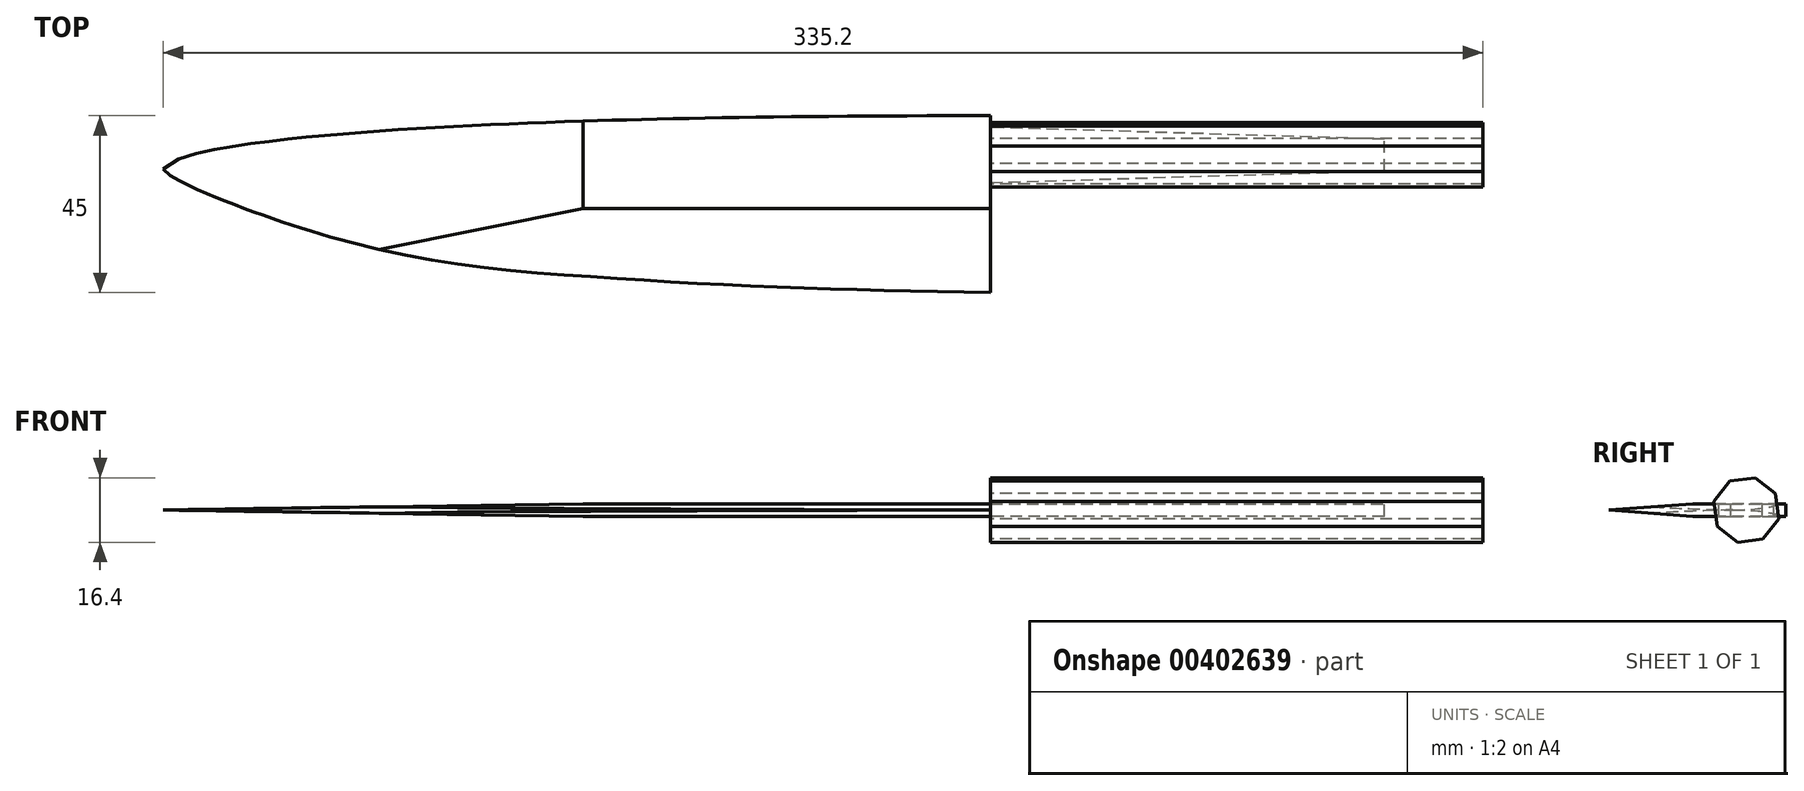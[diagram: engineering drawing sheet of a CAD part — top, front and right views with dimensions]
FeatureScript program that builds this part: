
annotation { "Feature Type Name" : "Feature", "Feature Type Description" : "" }
export const myFeature = defineFeature(function(context is Context, id is Id, definition is map)
    precondition{}
    {
        {
            var Q0;
            Q0=qCreatedBy(makeId("Top.planeOp"),FACE);
            var sketch = newSketch(context, id + "F0", { "sketchPlane" : qUnion([Q0])});
            skFitSpline(sketch, "E0", {"points": [v(0, 17) * mm, v(-209.96, 4) * mm, v(-210, 3) * mm, v(-163.2, -15.06) * mm, v(-98.97, -24.11) * mm, v(0, -28) * mm], "startDerivative": vector(-1422.34, 0) * mm, "endDerivative": vector(667.4, -12.24) * mm});
            skLineSegment(sketch, "E1", {"start": v(0, -28) * mm, "end": v(0, 0) * mm});
            skLineSegment(sketch, "E2", {"start": v(0, 0) * mm, "end": v(100, 3) * mm});
            skLineSegment(sketch, "E3", {"start": v(100, 3) * mm, "end": v(100, 11) * mm});
            skLineSegment(sketch, "E4", {"start": v(100, 11) * mm, "end": v(0, 14) * mm});
            skLineSegment(sketch, "E5", {"start": v(0, 14) * mm, "end": v(0, 17) * mm});
            skSolve(sketch);
        }
        {
            var Q0;
            Q0=makeQuery(id+"F0.imprint","IMPRINT",FACE,{"disambiguationData":[TD([[makeQuery(id+"F0.imprint","IMPRINT",EDGE,{"derivedFrom":sQuery(id+"F0.wireOp",EDGE,"E0")}),1.0]])]});
            extrude(context, id + "F1", {"entities" : qUnion([Q0]), "endBound" : BoundingType.SYMMETRIC, "oppositeDirection" : true, "depth" : 3.2 * mm});
        }
        {
            var Q0;
            Q0=makeQuery(id+"F1.opExtrude","SWEPT_FACE",FACE,{"disambiguationData":[OSD([sQuery(id+"F0.wireOp",EDGE,"E1")])]});
            var sketch = newSketch(context, id + "F2", { "sketchPlane" : qUnion([Q0])});
            skLineSegment(sketch, "E6", {"start": v(-28, 0) * mm, "end": v(-6.6, 1.6) * mm});
            skLineSegment(sketch, "E7", {"start": v(-28, 0) * mm, "end": v(-6.6, -1.6) * mm});
            skLineSegment(sketch, "E8", {"start": v(-6.6, 1.6) * mm, "end": v(-6.6, 8.5) * mm});
            skLineSegment(sketch, "E9", {"start": v(-6.6, 8.5) * mm, "end": v(-41.27, 6.96) * mm});
            skLineSegment(sketch, "E10", {"start": v(-41.27, 6.96) * mm, "end": v(-40.34, -14.06) * mm});
            skLineSegment(sketch, "E11", {"start": v(-40.34, -14.06) * mm, "end": v(-6.6, -11.1) * mm});
            skLineSegment(sketch, "E12", {"start": v(-6.6, -11.1) * mm, "end": v(-6.6, -1.6) * mm});
            skSolve(sketch);
        }
        {
            var Q0;
            Q0 = qSketchRegion(id + "F2", true);
            extrude(context, id + "F3", {"entities" : qUnion([Q0]), "operationType" : NewBodyOperationType.REMOVE, "endBound" : BoundingType.THROUGH_ALL, "oppositeDirection" : true, "depth" : 25 * mm});
        }
        {
            var Q0;
            Q0=qCreatedBy(makeId("Front.planeOp"),FACE);
            var sketch = newSketch(context, id + "F4", { "sketchPlane" : qUnion([Q0])});
            skFitSpline(sketch, "E13.0", {"points": [v(0, 1.6) * mm, v(-70.11, 1.6) * mm, v(-140.23, 1.6) * mm, v(-210.34, 1.6) * mm]});
            skFitSpline(sketch, "E14.0", {"points": [v(0, -1.6) * mm, v(-70.11, -1.6) * mm, v(-140.23, -1.6) * mm, v(-210.34, -1.6) * mm]});
            skLineSegment(sketch, "E15", {"start": v(0, 1.6) * mm, "end": v(-103.5, 1.6) * mm});
            skLineSegment(sketch, "E16", {"start": v(-103.5, 1.6) * mm, "end": v(-210.2, 0) * mm});
            skLineSegment(sketch, "E17", {"start": v(-210.2, 0) * mm, "end": v(-103.5, -1.6) * mm});
            skLineSegment(sketch, "E18", {"start": v(-103.5, -1.6) * mm, "end": v(-103.5, -14.4) * mm});
            skLineSegment(sketch, "E19", {"start": v(-103.5, -14.4) * mm, "end": v(-238.36, -17.8) * mm});
            skLineSegment(sketch, "E20", {"start": v(-238.36, -17.8) * mm, "end": v(-239.4, 23.74) * mm});
            skLineSegment(sketch, "E21", {"start": v(-239.4, 23.74) * mm, "end": v(-103.5, 23.74) * mm});
            skLineSegment(sketch, "E22", {"start": v(-103.5, 23.74) * mm, "end": v(-103.5, 1.6) * mm});
            skSolve(sketch);
        }
        {
            var Q0;
            Q0=makeQuery(id+"F4.imprint","IMPRINT",FACE,{"disambiguationData":[TD([[makeQuery(id+"F4.imprint","IMPRINT",EDGE,{"derivedFrom":sQuery(id+"F4.wireOp",EDGE,"E16")}),-1.0]])]});
            extrude(context, id + "F5", {"entities" : qUnion([Q0]), "operationType" : NewBodyOperationType.REMOVE, "endBound" : BoundingType.SYMMETRIC, "oppositeDirection" : true, "depth" : 60 * mm});
        }
        {
            var Q0;
            Q0=qCreatedBy(makeId("Right.planeOp"),FACE);
            var sketch = newSketch(context, id + "F6", { "sketchPlane" : qUnion([Q0])});
            skCircle(sketch, "E23.cCircle", {"center": v(7, 0) * mm, "radius": 8.5 * mm, "construction": true});
            skLineSegment(sketch, "E23.0", {"start": v(14.37, 4.23) * mm, "end": v(15.2, -2.22) * mm});
            skLineSegment(sketch, "E23.1", {"start": v(15.2, -2.22) * mm, "end": v(11.23, -7.37) * mm});
            skLineSegment(sketch, "E23.2", {"start": v(11.23, -7.37) * mm, "end": v(4.78, -8.2) * mm});
            skLineSegment(sketch, "E23.3", {"start": v(4.78, -8.2) * mm, "end": v(-0.37, -4.23) * mm});
            skLineSegment(sketch, "E23.4", {"start": v(-0.37, -4.23) * mm, "end": v(-1.2, 2.22) * mm});
            skLineSegment(sketch, "E23.5", {"start": v(-1.2, 2.22) * mm, "end": v(2.77, 7.37) * mm});
            skLineSegment(sketch, "E23.6", {"start": v(2.77, 7.37) * mm, "end": v(9.22, 8.2) * mm});
            skLineSegment(sketch, "E23.7", {"start": v(9.22, 8.2) * mm, "end": v(14.37, 4.23) * mm});
            skSolve(sketch);
        }
        {
            var Q0;
            Q0=makeQuery(id+"F6.imprint","IMPRINT",FACE,{"disambiguationData":[TD([[makeQuery(id+"F6.imprint","IMPRINT",EDGE,{"derivedFrom":sQuery(id+"F6.wireOp",EDGE,"E23.0")}),-1.0]])]});
            extrude(context, id + "F7", {"entities" : qUnion([Q0]), "depth" : 125 * mm});
        }
    });
